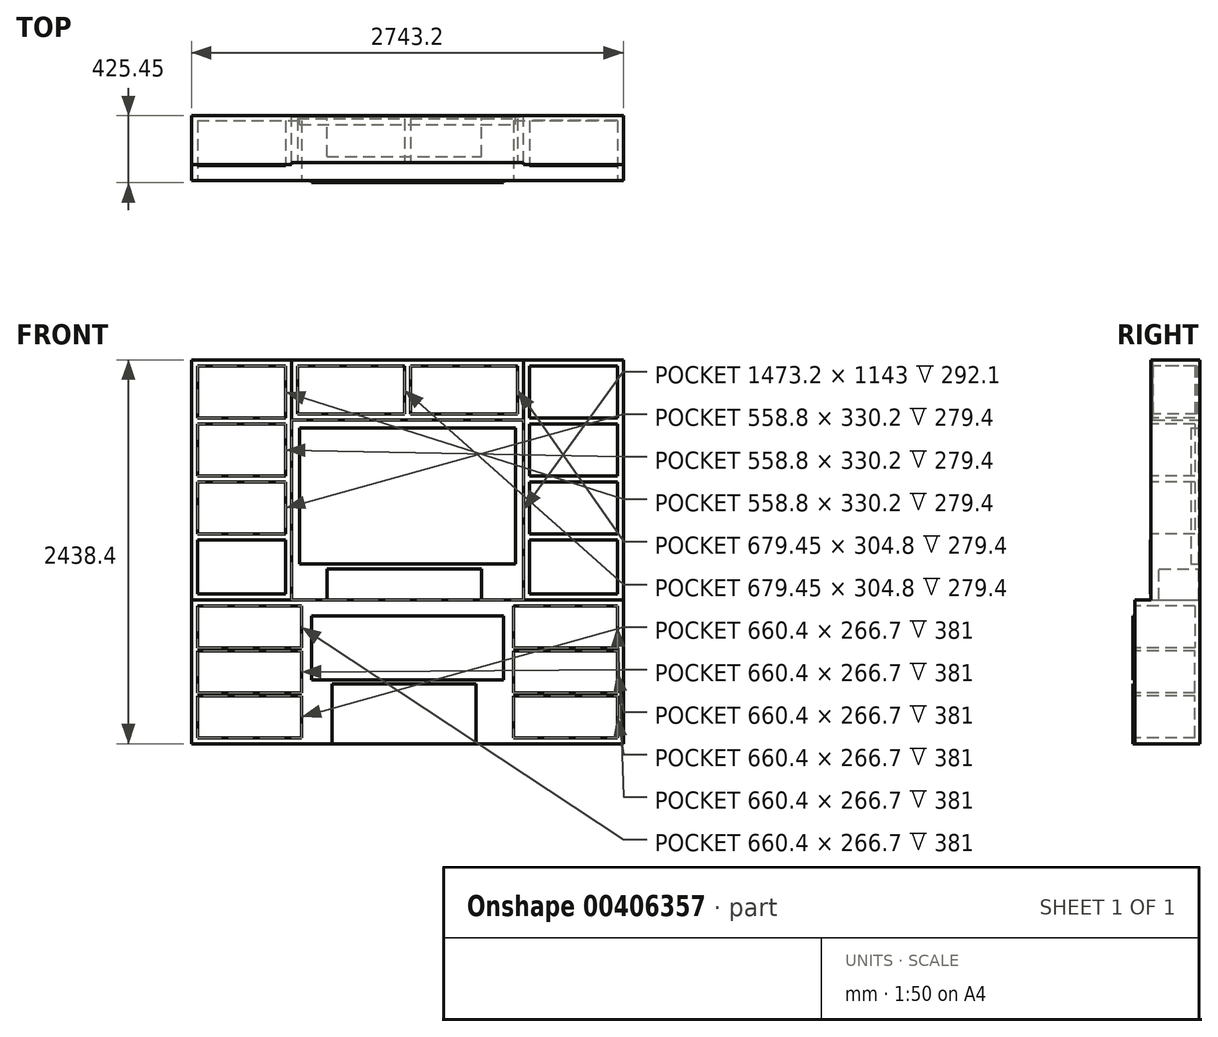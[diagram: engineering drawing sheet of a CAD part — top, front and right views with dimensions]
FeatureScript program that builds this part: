
annotation { "Feature Type Name" : "Feature", "Feature Type Description" : "" }
export const myFeature = defineFeature(function(context is Context, id is Id, definition is map)
    precondition{}
    {
        {
            var Q0;
            Q0=qCreatedBy(makeId("Front.planeOp"),FACE);
            var sketch = newSketch(context, id + "F0", { "sketchPlane" : qUnion([Q0]), "disableImprinting" : false});
            skLineSegment(sketch, "E0.bottom", {"start": v(0, 0) * mm, "end": v(2743.2, 0) * mm});
            skLineSegment(sketch, "E0.top", {"start": v(0, 2438.4) * mm, "end": v(2743.2, 2438.4) * mm});
            skLineSegment(sketch, "E0.left", {"start": v(0, 0) * mm, "end": v(0, 2438.4) * mm});
            skLineSegment(sketch, "E0.right", {"start": v(2743.2, 0) * mm, "end": v(2743.2, 2438.4) * mm});
            skSolve(sketch);
        }
        {
            var Q0;
            Q0 = qSketchRegion(id + "F0", true);
            extrude(context, id + "F1", {"entities" : qUnion([Q0]), "flatOperationType" : FlatOperationType.REMOVE, "offsetDistance" : 25.4 * mm, "depth" : 6.35 * mm, "domain" : OperationDomain.MODEL});
        }
        {
            var Q0;
            Q0=makeQuery(id+"F1.opExtrude","CAP_FACE",FACE,{"disambiguationData":[OSD([sQuery(id+"F0.wireOp",EDGE,"E0.bottom"),sQuery(id+"F0.wireOp",EDGE,"E0.top"),sQuery(id+"F0.wireOp",EDGE,"E0.left"),sQuery(id+"F0.wireOp",EDGE,"E0.right")])],"isStart":false});
            var sketch = newSketch(context, id + "F2", { "sketchPlane" : qUnion([Q0])});
            skLineSegment(sketch, "E1.bottom", {"start": v(0, 0) * mm, "end": v(2743.2, 0) * mm});
            skLineSegment(sketch, "E1.top", {"start": v(0, 914.4) * mm, "end": v(2743.2, 914.4) * mm});
            skLineSegment(sketch, "E1.left", {"start": v(0, 0) * mm, "end": v(0, 914.4) * mm});
            skLineSegment(sketch, "E1.right", {"start": v(2743.2, 0) * mm, "end": v(2743.2, 914.4) * mm});
            skSolve(sketch);
        }
        {
            var Q0;
            Q0 = qSketchRegion(id + "F2", true);
            extrude(context, id + "F3", {"entities" : qUnion([Q0]), "operationType" : NewBodyOperationType.ADD, "flatOperationType" : FlatOperationType.REMOVE, "offsetDistance" : 25.4 * mm, "depth" : 406.4 * mm, "domain" : OperationDomain.MODEL});
        }
        {
            var Q0;
            Q0=makeQuery(id+"F1.opExtrude","CAP_FACE",FACE,{"disambiguationData":[OSD([sQuery(id+"F0.wireOp",EDGE,"E0.bottom"),sQuery(id+"F0.wireOp",EDGE,"E0.top"),sQuery(id+"F0.wireOp",EDGE,"E0.left"),sQuery(id+"F0.wireOp",EDGE,"E0.right")])],"isStart":false});
            var sketch = newSketch(context, id + "F4", { "sketchPlane" : qUnion([Q0])});
            skLineSegment(sketch, "E2.bottom", {"start": v(0, 914.4) * mm, "end": v(635, 914.4) * mm});
            skLineSegment(sketch, "E2.top", {"start": v(0, 2438.4) * mm, "end": v(635, 2438.4) * mm});
            skLineSegment(sketch, "E2.left", {"start": v(0, 914.4) * mm, "end": v(0, 2438.4) * mm});
            skLineSegment(sketch, "E2.right", {"start": v(635, 914.4) * mm, "end": v(635, 2438.4) * mm});
            skLineSegment(sketch, "E3.bottom", {"start": v(2743.2, 914.4) * mm, "end": v(2108.2, 914.4) * mm});
            skLineSegment(sketch, "E3.top", {"start": v(2743.2, 2438.4) * mm, "end": v(2108.2, 2438.4) * mm});
            skLineSegment(sketch, "E3.left", {"start": v(2743.2, 914.4) * mm, "end": v(2743.2, 2438.4) * mm});
            skLineSegment(sketch, "E3.right", {"start": v(2108.2, 914.4) * mm, "end": v(2108.2, 2438.4) * mm});
            skSolve(sketch);
        }
        {
            var Q0;
            Q0 = qSketchRegion(id + "F4", true);
            extrude(context, id + "F5", {"entities" : qUnion([Q0]), "operationType" : NewBodyOperationType.ADD, "flatOperationType" : FlatOperationType.REMOVE, "offsetDistance" : 25.4 * mm, "depth" : 304.8 * mm, "domain" : OperationDomain.MODEL});
        }
        {
            var Q0;
            Q0=makeQuery(id+"F1.opExtrude","CAP_FACE",FACE,{"disambiguationData":[OSD([sQuery(id+"F0.wireOp",EDGE,"E0.bottom"),sQuery(id+"F0.wireOp",EDGE,"E0.top"),sQuery(id+"F0.wireOp",EDGE,"E0.left"),sQuery(id+"F0.wireOp",EDGE,"E0.right")])],"isStart":false});
            var sketch = newSketch(context, id + "F6", { "sketchPlane" : qUnion([Q0])});
            skLineSegment(sketch, "E4.bottom", {"start": v(635, 2438.4) * mm, "end": v(2108.2, 2438.4) * mm});
            skLineSegment(sketch, "E4.top", {"start": v(635, 2057.4) * mm, "end": v(2108.2, 2057.4) * mm});
            skLineSegment(sketch, "E4.left", {"start": v(635, 2438.4) * mm, "end": v(635, 2057.4) * mm});
            skLineSegment(sketch, "E4.right", {"start": v(2108.2, 2438.4) * mm, "end": v(2108.2, 2057.4) * mm});
            skSolve(sketch);
        }
        {
            var Q0;
            Q0 = qSketchRegion(id + "F6", true);
            extrude(context, id + "F7", {"entities" : qUnion([Q0]), "operationType" : NewBodyOperationType.ADD, "flatOperationType" : FlatOperationType.REMOVE, "offsetDistance" : 25.4 * mm, "depth" : 292.1 * mm, "domain" : OperationDomain.MODEL});
        }
        {
            var Q0;
            Q0=makeQuery(id+"F5.opExtrude","CAP_FACE",FACE,{"disambiguationData":[OSD([sQuery(id+"F4.wireOp",EDGE,"E2.bottom"),sQuery(id+"F4.wireOp",EDGE,"E2.top"),sQuery(id+"F4.wireOp",EDGE,"E2.left"),sQuery(id+"F4.wireOp",EDGE,"E2.right")])],"isStart":false});
            var sketch = newSketch(context, id + "F8", { "sketchPlane" : qUnion([Q0])});
            skLineSegment(sketch, "E5.bottom", {"start": v(38.1, 2400.3) * mm, "end": v(596.9, 2400.3) * mm});
            skLineSegment(sketch, "E5.top", {"start": v(38.1, 2070.1) * mm, "end": v(596.9, 2070.1) * mm});
            skLineSegment(sketch, "E5.left", {"start": v(38.1, 2400.3) * mm, "end": v(38.1, 2070.1) * mm});
            skLineSegment(sketch, "E5.right", {"start": v(596.9, 2400.3) * mm, "end": v(596.9, 2070.1) * mm});
            skLineSegment(sketch, "E6.bottom", {"start": v(38.1, 2032) * mm, "end": v(596.9, 2032) * mm});
            skLineSegment(sketch, "E6.top", {"start": v(38.1, 1701.8) * mm, "end": v(596.9, 1701.8) * mm});
            skLineSegment(sketch, "E6.left", {"start": v(38.1, 2032) * mm, "end": v(38.1, 1701.8) * mm});
            skLineSegment(sketch, "E6.right", {"start": v(596.9, 2032) * mm, "end": v(596.9, 1701.8) * mm});
            skLineSegment(sketch, "E7.bottom", {"start": v(38.1, 1663.7) * mm, "end": v(596.9, 1663.7) * mm});
            skLineSegment(sketch, "E7.top", {"start": v(38.1, 1333.5) * mm, "end": v(596.9, 1333.5) * mm});
            skLineSegment(sketch, "E7.left", {"start": v(38.1, 1663.7) * mm, "end": v(38.1, 1333.5) * mm});
            skLineSegment(sketch, "E7.right", {"start": v(596.9, 1663.7) * mm, "end": v(596.9, 1333.5) * mm});
            skLineSegment(sketch, "E8", {"start": v(1371.6, 0) * mm, "end": v(1371.6, 2465.76) * mm, "construction": true});
            skLineSegment(sketch, "E9.MirrorCS", {"start": v(2705.1, 2032) * mm, "end": v(2146.3, 2032) * mm});
            skLineSegment(sketch, "E10.MirrorCS", {"start": v(2146.3, 2400.3) * mm, "end": v(2146.3, 2070.1) * mm});
            skLineSegment(sketch, "E11.MirrorCS", {"start": v(2705.1, 2400.3) * mm, "end": v(2705.1, 2070.1) * mm});
            skLineSegment(sketch, "E12.MirrorCS", {"start": v(2705.1, 2070.1) * mm, "end": v(2146.3, 2070.1) * mm});
            skLineSegment(sketch, "E13.MirrorCS", {"start": v(2705.1, 1333.5) * mm, "end": v(2146.3, 1333.5) * mm});
            skLineSegment(sketch, "E14.MirrorCS", {"start": v(2705.1, 1663.7) * mm, "end": v(2146.3, 1663.7) * mm});
            skLineSegment(sketch, "E15.MirrorCS", {"start": v(2146.3, 2032) * mm, "end": v(2146.3, 1701.8) * mm});
            skLineSegment(sketch, "E16.MirrorCS", {"start": v(2705.1, 2032) * mm, "end": v(2705.1, 1701.8) * mm});
            skLineSegment(sketch, "E17.MirrorCS", {"start": v(2705.1, 1701.8) * mm, "end": v(2146.3, 1701.8) * mm});
            skLineSegment(sketch, "E18.MirrorCS", {"start": v(2705.1, 1663.7) * mm, "end": v(2705.1, 1333.5) * mm});
            skLineSegment(sketch, "E19.MirrorCS", {"start": v(2146.3, 1663.7) * mm, "end": v(2146.3, 1333.5) * mm});
            skLineSegment(sketch, "E20.MirrorCS", {"start": v(2705.1, 2400.3) * mm, "end": v(2146.3, 2400.3) * mm});
            skSolve(sketch);
        }
        {
            var Q0;
            Q0 = qSketchRegion(id + "F8", true);
            extrude(context, id + "F9", {"entities" : qUnion([Q0]), "operationType" : NewBodyOperationType.REMOVE, "oppositeDirection" : true, "depth" : 279.4 * mm});
        }
        {
            var Q0;
            Q0=makeQuery(id+"F7.opExtrude","CAP_FACE",FACE,{"disambiguationData":[OSD([sQuery(id+"F6.wireOp",EDGE,"E4.bottom"),sQuery(id+"F6.wireOp",EDGE,"E4.top"),sQuery(id+"F6.wireOp",EDGE,"E4.left"),sQuery(id+"F6.wireOp",EDGE,"E4.right")])],"isStart":false});
            var sketch = newSketch(context, id + "F10", { "sketchPlane" : qUnion([Q0])});
            skLineSegment(sketch, "E21.bottom", {"start": v(673.1, 2400.3) * mm, "end": v(1352.55, 2400.3) * mm});
            skLineSegment(sketch, "E21.top", {"start": v(673.1, 2095.5) * mm, "end": v(1352.55, 2095.5) * mm});
            skLineSegment(sketch, "E21.left", {"start": v(673.1, 2400.3) * mm, "end": v(673.1, 2095.5) * mm});
            skLineSegment(sketch, "E21.right", {"start": v(1352.55, 2400.3) * mm, "end": v(1352.55, 2095.5) * mm});
            skLineSegment(sketch, "E22.bottom", {"start": v(1390.65, 2400.3) * mm, "end": v(2070.1, 2400.3) * mm});
            skLineSegment(sketch, "E22.top", {"start": v(1390.65, 2095.5) * mm, "end": v(2070.1, 2095.5) * mm});
            skLineSegment(sketch, "E22.left", {"start": v(1390.65, 2400.3) * mm, "end": v(1390.65, 2095.5) * mm});
            skLineSegment(sketch, "E22.right", {"start": v(2070.1, 2400.3) * mm, "end": v(2070.1, 2095.5) * mm});
            skSolve(sketch);
        }
        {
            var Q0;
            Q0 = qSketchRegion(id + "F10", true);
            extrude(context, id + "F11", {"entities" : qUnion([Q0]), "operationType" : NewBodyOperationType.REMOVE, "oppositeDirection" : true, "depth" : 279.4 * mm});
        }
        {
            var Q0;
            Q0=makeQuery(id+"F1.opExtrude","CAP_FACE",FACE,{"disambiguationData":[OSD([sQuery(id+"F0.wireOp",EDGE,"E0.bottom"),sQuery(id+"F0.wireOp",EDGE,"E0.top"),sQuery(id+"F0.wireOp",EDGE,"E0.left"),sQuery(id+"F0.wireOp",EDGE,"E0.right")])],"isStart":false});
            var sketch = newSketch(context, id + "F12", { "sketchPlane" : qUnion([Q0])});
            skLineSegment(sketch, "E23.bottom", {"start": v(685.8, 2006.6) * mm, "end": v(2057.4, 2006.6) * mm});
            skLineSegment(sketch, "E23.top", {"start": v(685.8, 1143) * mm, "end": v(2057.4, 1143) * mm});
            skLineSegment(sketch, "E23.left", {"start": v(685.8, 2006.6) * mm, "end": v(685.8, 1143) * mm});
            skLineSegment(sketch, "E23.right", {"start": v(2057.4, 2006.6) * mm, "end": v(2057.4, 1143) * mm});
            skSolve(sketch);
        }
        {
            var Q0;
            Q0 = qSketchRegion(id + "F12", true);
            extrude(context, id + "F13", {"entities" : qUnion([Q0]), "depth" : 50.8 * mm});
        }
        {
            var Q0;
            Q0=makeQuery(id+"F5.opExtrude","CAP_FACE",FACE,{"disambiguationData":[OSD([sQuery(id+"F4.wireOp",EDGE,"E2.bottom"),sQuery(id+"F4.wireOp",EDGE,"E2.top"),sQuery(id+"F4.wireOp",EDGE,"E2.left"),sQuery(id+"F4.wireOp",EDGE,"E2.right")])],"isStart":false});
            var sketch = newSketch(context, id + "F14", { "sketchPlane" : qUnion([Q0])});
            skLineSegment(sketch, "E24.bottom", {"start": v(38.1, 952.5) * mm, "end": v(596.9, 952.5) * mm});
            skLineSegment(sketch, "E24.top", {"start": v(38.1, 1295.4) * mm, "end": v(596.9, 1295.4) * mm});
            skLineSegment(sketch, "E24.left", {"start": v(38.1, 952.5) * mm, "end": v(38.1, 1295.4) * mm});
            skLineSegment(sketch, "E24.right", {"start": v(596.9, 952.5) * mm, "end": v(596.9, 1295.4) * mm});
            skLineSegment(sketch, "E25.bottom", {"start": v(2146.3, 952.5) * mm, "end": v(2705.1, 952.5) * mm});
            skLineSegment(sketch, "E25.top", {"start": v(2146.3, 1295.4) * mm, "end": v(2705.1, 1295.4) * mm});
            skLineSegment(sketch, "E25.left", {"start": v(2146.3, 952.5) * mm, "end": v(2146.3, 1295.4) * mm});
            skLineSegment(sketch, "E25.right", {"start": v(2705.1, 952.5) * mm, "end": v(2705.1, 1295.4) * mm});
            skSolve(sketch);
        }
        {
            var Q0;
            Q0 = qSketchRegion(id + "F14", true);
            extrude(context, id + "F15", {"entities" : qUnion([Q0]), "depth" : 5.08 * mm});
        }
        {
            var Q0;
            Q0=makeQuery(id+"F3.opExtrude","CAP_FACE",FACE,{"disambiguationData":[OSD([sQuery(id+"F2.wireOp",EDGE,"E1.bottom"),sQuery(id+"F2.wireOp",EDGE,"E1.top"),sQuery(id+"F2.wireOp",EDGE,"E1.left"),sQuery(id+"F2.wireOp",EDGE,"E1.right")])],"isStart":false});
            var sketch = newSketch(context, id + "F16", { "sketchPlane" : qUnion([Q0])});
            skLineSegment(sketch, "E26.bottom", {"start": v(762, 812.8) * mm, "end": v(1981.2, 812.8) * mm});
            skLineSegment(sketch, "E26.top", {"start": v(762, 406.4) * mm, "end": v(1981.2, 406.4) * mm});
            skLineSegment(sketch, "E26.left", {"start": v(762, 812.8) * mm, "end": v(762, 406.4) * mm});
            skLineSegment(sketch, "E26.right", {"start": v(1981.2, 812.8) * mm, "end": v(1981.2, 406.4) * mm});
            skSolve(sketch);
        }
        {
            var Q0;
            Q0=makeQuery(id+"F1.opExtrude","CAP_FACE",FACE,{"disambiguationData":[OSD([sQuery(id+"F0.wireOp",EDGE,"E0.bottom"),sQuery(id+"F0.wireOp",EDGE,"E0.top"),sQuery(id+"F0.wireOp",EDGE,"E0.left"),sQuery(id+"F0.wireOp",EDGE,"E0.right")])],"isStart":false});
            var sketch = newSketch(context, id + "F17", { "sketchPlane" : qUnion([Q0])});
            skLineSegment(sketch, "E27.bottom", {"start": v(861.1, 914.4) * mm, "end": v(1842.14, 914.4) * mm});
            skLineSegment(sketch, "E27.top", {"start": v(861.1, 1109.29) * mm, "end": v(1842.14, 1109.29) * mm});
            skLineSegment(sketch, "E27.left", {"start": v(861.1, 914.4) * mm, "end": v(861.1, 1109.29) * mm});
            skLineSegment(sketch, "E27.right", {"start": v(1842.14, 914.4) * mm, "end": v(1842.14, 1109.29) * mm});
            skSolve(sketch);
        }
        {
            var Q0;
            Q0 = qSketchRegion(id + "F17", true);
            extrude(context, id + "F18", {"entities" : qUnion([Q0]), "depth" : 254 * mm});
        }
        {
            var Q0;
            Q0 = qSketchRegion(id + "F16", true);
            extrude(context, id + "F19", {"entities" : qUnion([Q0]), "depth" : 12.7 * mm});
        }
        {
            var Q0;
            Q0=makeQuery(id+"F3.opExtrude","CAP_FACE",FACE,{"disambiguationData":[OSD([sQuery(id+"F2.wireOp",EDGE,"E1.bottom"),sQuery(id+"F2.wireOp",EDGE,"E1.top"),sQuery(id+"F2.wireOp",EDGE,"E1.left"),sQuery(id+"F2.wireOp",EDGE,"E1.right")])],"isStart":false});
            var sketch = newSketch(context, id + "F20", { "sketchPlane" : qUnion([Q0])});
            skLineSegment(sketch, "E28.bottom", {"start": v(892.37, 0) * mm, "end": v(1806.77, 0) * mm});
            skLineSegment(sketch, "E28.top", {"start": v(892.37, 381) * mm, "end": v(1806.77, 381) * mm});
            skLineSegment(sketch, "E28.left", {"start": v(892.37, 0) * mm, "end": v(892.37, 381) * mm});
            skLineSegment(sketch, "E28.right", {"start": v(1806.77, 0) * mm, "end": v(1806.77, 381) * mm});
            skSolve(sketch);
        }
        {
            var Q0;
            Q0 = qSketchRegion(id + "F20", true);
            extrude(context, id + "F21", {"entities" : qUnion([Q0]), "depth" : 12.7 * mm});
        }
        {
            var Q0;
            Q0=makeQuery(id+"F3.opExtrude","CAP_FACE",FACE,{"disambiguationData":[OSD([sQuery(id+"F2.wireOp",EDGE,"E1.bottom"),sQuery(id+"F2.wireOp",EDGE,"E1.top"),sQuery(id+"F2.wireOp",EDGE,"E1.left"),sQuery(id+"F2.wireOp",EDGE,"E1.right")])],"isStart":false});
            var sketch = newSketch(context, id + "F22", { "sketchPlane" : qUnion([Q0])});
            skLineSegment(sketch, "E29.bottom", {"start": v(38.1, 38.1) * mm, "end": v(698.5, 38.1) * mm});
            skLineSegment(sketch, "E29.top", {"start": v(38.1, 876.3) * mm, "end": v(698.5, 876.3) * mm});
            skLineSegment(sketch, "E29.left", {"start": v(38.1, 38.1) * mm, "end": v(38.1, 304.8) * mm});
            skLineSegment(sketch, "E29.right", {"start": v(698.5, 38.1) * mm, "end": v(698.5, 304.8) * mm});
            skLineSegment(sketch, "E30.bottom", {"start": v(2705.1, 876.3) * mm, "end": v(2044.7, 876.3) * mm});
            skLineSegment(sketch, "E30.top", {"start": v(2705.1, 38.1) * mm, "end": v(2044.7, 38.1) * mm});
            skLineSegment(sketch, "E30.left", {"start": v(2705.1, 876.3) * mm, "end": v(2705.1, 609.6) * mm});
            skLineSegment(sketch, "E30.right", {"start": v(2044.7, 876.3) * mm, "end": v(2044.7, 609.6) * mm});
            skLineSegment(sketch, "E31", {"start": v(2044.7, 609.6) * mm, "end": v(2705.1, 609.6) * mm});
            skLineSegment(sketch, "E32", {"start": v(2044.7, 590.55) * mm, "end": v(2705.1, 590.55) * mm});
            skLineSegment(sketch, "E33", {"start": v(2044.7, 323.85) * mm, "end": v(2705.1, 323.85) * mm});
            skLineSegment(sketch, "E34", {"start": v(2044.7, 304.8) * mm, "end": v(2705.1, 304.8) * mm});
            skLineSegment(sketch, "E35.trimOffspring", {"start": v(2044.7, 590.55) * mm, "end": v(2044.7, 323.85) * mm});
            skLineSegment(sketch, "E36.trimOffspring", {"start": v(2705.1, 590.55) * mm, "end": v(2705.1, 323.85) * mm});
            skLineSegment(sketch, "E37.trimOffspring", {"start": v(2044.7, 304.8) * mm, "end": v(2044.7, 38.1) * mm});
            skLineSegment(sketch, "E38.trimOffspring", {"start": v(2705.1, 304.8) * mm, "end": v(2705.1, 38.1) * mm});
            skLineSegment(sketch, "E39", {"start": v(38.1, 609.6) * mm, "end": v(698.5, 609.6) * mm});
            skLineSegment(sketch, "E40", {"start": v(38.1, 590.55) * mm, "end": v(698.5, 590.55) * mm});
            skLineSegment(sketch, "E41", {"start": v(38.1, 323.85) * mm, "end": v(698.5, 323.85) * mm});
            skLineSegment(sketch, "E42", {"start": v(38.1, 304.8) * mm, "end": v(698.5, 304.8) * mm});
            skLineSegment(sketch, "E43.trimOffspring", {"start": v(38.1, 609.6) * mm, "end": v(38.1, 876.3) * mm});
            skLineSegment(sketch, "E44.trimOffspring", {"start": v(698.5, 609.6) * mm, "end": v(698.5, 876.3) * mm});
            skLineSegment(sketch, "E45.trimOffspring", {"start": v(698.5, 323.85) * mm, "end": v(698.5, 590.55) * mm});
            skLineSegment(sketch, "E46.trimOffspring", {"start": v(38.1, 323.85) * mm, "end": v(38.1, 590.55) * mm});
            skSolve(sketch);
        }
        {
            var Q0;
            Q0 = qSketchRegion(id + "F22", true);
            extrude(context, id + "F23", {"entities" : qUnion([Q0]), "operationType" : NewBodyOperationType.REMOVE, "oppositeDirection" : true, "depth" : 381 * mm});
        }
    });
